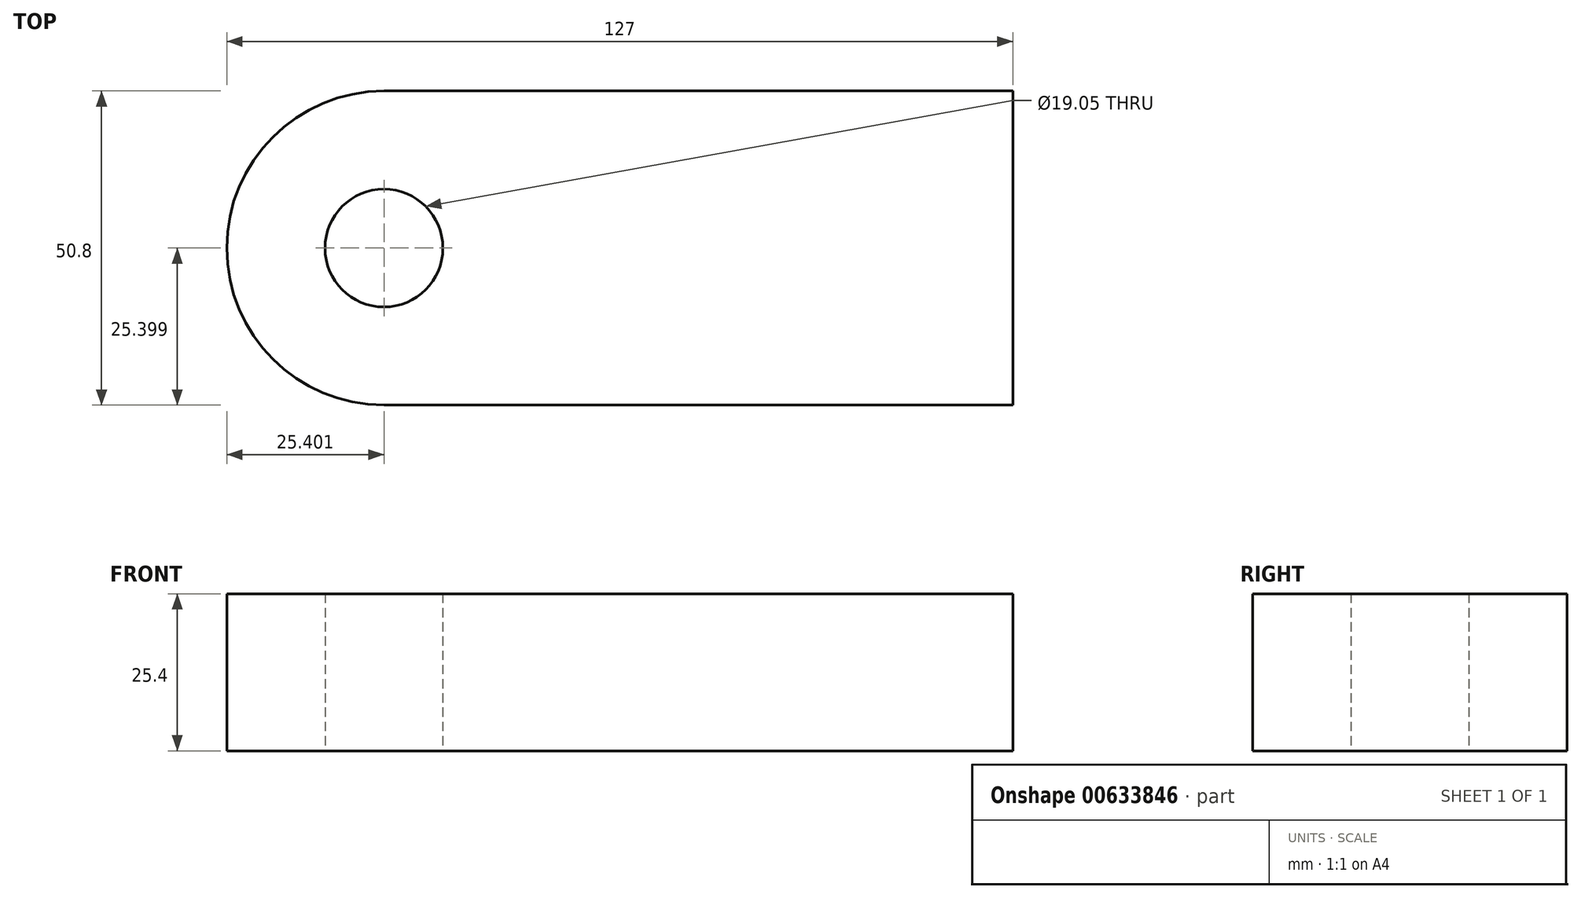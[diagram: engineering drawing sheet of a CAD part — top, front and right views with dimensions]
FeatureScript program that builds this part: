
annotation { "Feature Type Name" : "Feature", "Feature Type Description" : "" }
export const myFeature = defineFeature(function(context is Context, id is Id, definition is map)
    precondition{}
    {
        {
            var Q0;
            Q0=qCreatedBy(makeId("Top.planeOp"),FACE);
            var sketch = newSketch(context, id + "F0", { "sketchPlane" : qUnion([Q0])});
            skLineSegment(sketch, "E0", {"start": v(-38.63, 32.87) * mm, "end": v(62.97, 32.87) * mm});
            skLineSegment(sketch, "E1", {"start": v(62.97, 32.87) * mm, "end": v(62.97, -17.93) * mm});
            skLineSegment(sketch, "E2", {"start": v(62.97, -17.93) * mm, "end": v(-38.63, -17.93) * mm});
            skLineSegment(sketch, "E3", {"start": v(-38.63, 32.87) * mm, "end": v(-38.63, -17.93) * mm});
            skArc(sketch, "E4", {"start": v(-38.63, 32.87) * mm, "mid": v(-64.03, 7.47) * mm, "end": v(-38.63, -17.93) * mm});
            skCircle(sketch, "E5", {"center": v(-38.63, 7.47) * mm, "radius": 9.53 * mm});
            skSolve(sketch);
        }
        {
            var Q0;
            Q0 = qSketchRegion(id + "F0", true);
            extrude(context, id + "F1", {"entities" : qUnion([Q0]), "depth" : 25.4 * mm, "offsetDistance" : 25.4 * mm});
        }
    });
